# Revit family: Sanitary_Showers_hansgrohe_15586XXX-ShowerSelect-Comfort-Q-Thermost_new
name_source: partatom
category: Plumbing Fixtures
revit_build: Autodesk Revit 2018 (Build: 20170223_1515(x64)
units: mm (PartAtom-declared; Revit-internal decimal feet)

## family parameters
Always vertical = No
Cut with Voids When Loaded = No
OmniClass Number = 23.31.17.00
OmniClass Title = Showers
Part Type = Normal
Room Calculation Point = No
Round Connector Dimension = Use Diameter
Shared = No
Work Plane-Based = Yes

## types (5) — shared parameters
Always visible = Yes
BIMobject category = Showers
Default Elevation = 1219.2 mm  [stored 4 ft]
Description = ShowerSelect Comfort Q Thermostat for concealed installation for 2 functions with integrated security combination according to EN1717
Design country = Germany
Edition number = 1
IFC Classification = Sanitary Terminal
Manufacturer = Hansgrohe
Manufacturer country = Germany
Manufacturer name = hansgrohe
Masterformat 2014 Code = 22 41 23
Masterformat 2014 Description = Residential Showers
Model = 15586XXX
OmniClass Code = 23-31 17 00
OmniClass Description = Showers
Product Guid = 364a0258-ea64-4f0e-a93a-0cef407f3b76
Product SKU = 15586XXX
Product data url = https://bimobject.com
Product name = 15586XXX ShowerSelect Comfort Q Thermostat for concealed installation for 2 functions with integrated security combination according to EN1717
Product url = https://www.hansgrohe.com
QR code = https://bimobject.com
UNSPSC Code = 30181503
URL = https://www.hansgrohe.com
Uniclass 2015 Code = Pr_40_20_87_76
Uniclass 2015 Name = Shower heads
Uniformat II Code = D2010
Uniformat II Description = Plumbing Fixtures
Weight Net (Kg) = 2.3

## per-type parameters (varying)
| type | Material 1 |
| 700 Matte White | Hansgrohe - Metal - 700 Matte White |
| 670 Matte Black | Hansgrohe - Metal - 670 Matte Black |
| 340 Brushed Black Chrome | Hansgrohe - Metal - 340 Brushed Black Chrome |
| 140 Brushed Bronze | Hansgrohe - Metal - 140 Brushed Bronze |
| 000 Chrome | Hansgrohe - Metal - 000 Chrome |

note: [stored X ft] marks values corroborated as IEEE doubles in the binary element streams (Revit-internal decimal feet)

## geometry (parser evidence)
native form markers: Sweep x2
no freeform markers — native parametric forms only
